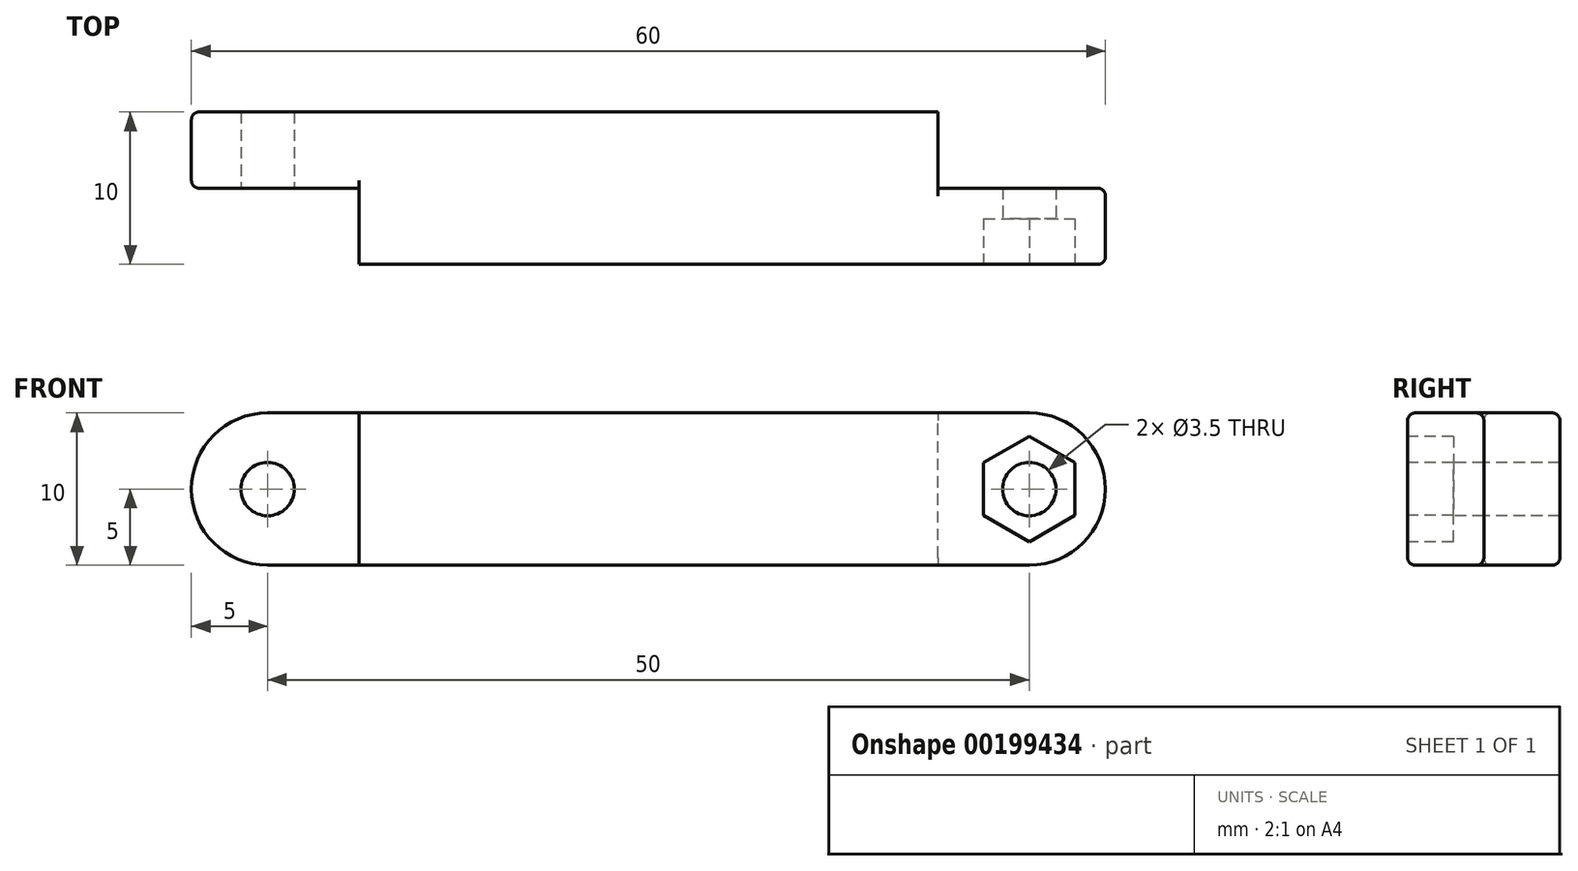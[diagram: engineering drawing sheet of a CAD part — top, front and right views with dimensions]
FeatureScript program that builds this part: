
annotation { "Feature Type Name" : "Feature", "Feature Type Description" : "" }
export const myFeature = defineFeature(function(context is Context, id is Id, definition is map)
    precondition{}
    {
        {
            var Q0;
            Q0=qCreatedBy(makeId("Front.planeOp"),FACE);
            var sketch = newSketch(context, id + "F0", { "sketchPlane" : qUnion([Q0])});
            skLineSegment(sketch, "E0.bottom", {"start": v(0, 0) * mm, "end": v(50, 0) * mm});
            skLineSegment(sketch, "E0.top", {"start": v(0, 10) * mm, "end": v(50, 10) * mm});
            skLineSegment(sketch, "E0.left", {"start": v(0, 0) * mm, "end": v(0, 10) * mm});
            skLineSegment(sketch, "E0.right", {"start": v(50, 0) * mm, "end": v(50, 10) * mm});
            skArc(sketch, "E1", {"start": v(0, 10) * mm, "mid": v(-5, 5) * mm, "end": v(0, 0) * mm});
            skArc(sketch, "E2", {"start": v(50, 0) * mm, "mid": v(55, 5) * mm, "end": v(50, 10) * mm});
            skSolve(sketch);
        }
        {
            var Q0;
            Q0 = qSketchRegion(id + "F0", true);
            extrude(context, id + "F1", {"entities" : qUnion([Q0]), "depth" : 10 * mm});
        }
        {
            var Q0;
            Q0=makeQuery(id+"F1.opExtrude","SWEPT_FACE",FACE,{"disambiguationData":[OSD([sQuery(id+"F0.wireOp",EDGE,"E0.top")])]});
            var sketch = newSketch(context, id + "F2", { "sketchPlane" : qUnion([Q0])});
            skLineSegment(sketch, "E3.bottom", {"start": v(-7.46, -5) * mm, "end": v(6, -5) * mm});
            skLineSegment(sketch, "E3.top", {"start": v(-7.46, -10) * mm, "end": v(6, -10) * mm});
            skLineSegment(sketch, "E3.left", {"start": v(-7.46, -5) * mm, "end": v(-7.46, -10) * mm});
            skLineSegment(sketch, "E3.right", {"start": v(6, -5) * mm, "end": v(6, -10) * mm});
            skLineSegment(sketch, "E4.bottom", {"start": v(44, -5) * mm, "end": v(57.28, -5) * mm});
            skLineSegment(sketch, "E4.top", {"start": v(44, 0) * mm, "end": v(57.28, 0) * mm});
            skLineSegment(sketch, "E4.left", {"start": v(44, 0) * mm, "end": v(44, -5) * mm});
            skLineSegment(sketch, "E4.right", {"start": v(57.28, 0) * mm, "end": v(57.28, -5) * mm});
            skSolve(sketch);
        }
        {
            var Q0;
            Q0 = qSketchRegion(id + "F2", true);
            extrude(context, id + "F3", {"entities" : qUnion([Q0]), "operationType" : NewBodyOperationType.REMOVE, "oppositeDirection" : true, "depth" : 25 * mm});
        }
        {
            var Q0;
            Q0=makeQuery(id+"F1.opExtrude","CAP_FACE",FACE,{"disambiguationData":[OSD([sQuery(id+"F0.wireOp",EDGE,"E0.bottom"),sQuery(id+"F0.wireOp",EDGE,"E0.top"),sQuery(id+"F0.wireOp",EDGE,"E1"),sQuery(id+"F0.wireOp",EDGE,"E2")])],"isStart":false});
            var sketch = newSketch(context, id + "F4", { "sketchPlane" : qUnion([Q0])});
            skCircle(sketch, "E5", {"center": v(50, 5) * mm, "radius": 1.75 * mm});
            skCircle(sketch, "E6", {"center": v(0, 5) * mm, "radius": 1.75 * mm});
            skPoint(sketch, "E6.centerSnap0", {"position": v(6, 5) * mm});
            skSolve(sketch);
        }
        {
            var Q0;
            Q0 = qSketchRegion(id + "F4", true);
            extrude(context, id + "F5", {"entities" : qUnion([Q0]), "operationType" : NewBodyOperationType.REMOVE, "oppositeDirection" : true, "depth" : 25 * mm});
        }
        {
            var Q0;
            Q0=makeQuery(id+"F1.opExtrude","CAP_FACE",FACE,{"disambiguationData":[OSD([sQuery(id+"F0.wireOp",EDGE,"E0.bottom"),sQuery(id+"F0.wireOp",EDGE,"E0.top"),sQuery(id+"F0.wireOp",EDGE,"E1"),sQuery(id+"F0.wireOp",EDGE,"E2")])],"isStart":false});
            var sketch = newSketch(context, id + "F6", { "sketchPlane" : qUnion([Q0])});
            skCircle(sketch, "E7.cCircle", {"center": v(50, 5) * mm, "radius": 3 * mm, "construction": true});
            skLineSegment(sketch, "E7.0", {"start": v(53, 6.73) * mm, "end": v(53, 3.27) * mm});
            skLineSegment(sketch, "E7.1", {"start": v(53, 3.27) * mm, "end": v(50, 1.54) * mm});
            skLineSegment(sketch, "E7.2", {"start": v(50, 1.54) * mm, "end": v(47, 3.27) * mm});
            skLineSegment(sketch, "E7.3", {"start": v(47, 3.27) * mm, "end": v(47, 6.73) * mm});
            skLineSegment(sketch, "E7.4", {"start": v(47, 6.73) * mm, "end": v(50, 8.46) * mm});
            skLineSegment(sketch, "E7.5", {"start": v(50, 8.46) * mm, "end": v(53, 6.73) * mm});
            skPoint(sketch, "E7.0.midPoint", {"position": v(53, 5) * mm});
            skSolve(sketch);
        }
        {
            var Q0;
            Q0 = qSketchRegion(id + "F6", true);
            extrude(context, id + "F7", {"entities" : qUnion([Q0]), "operationType" : NewBodyOperationType.REMOVE, "oppositeDirection" : true, "depth" : 3 * mm});
        }
        {
            var Q0;
            Q0=makeQuery(id+"F1.opExtrude","CAP_EDGE",EDGE,{"disambiguationData":[OSD([sQuery(id+"F0.wireOp",EDGE,"E0.top")])],"isStart":false});
            var Q1;
            Q1=makeQuery(id+"F1.opExtrude","CAP_EDGE",EDGE,{"disambiguationData":[OSD([sQuery(id+"F0.wireOp",EDGE,"E0.top")])],"isStart":true});
            var Q2;
            Q2=makeQuery(id+"F3.boolean.opBoolean","INTERSECT",EDGE,{"derivedFrom":[makeQuery(id+"F1.opExtrude","SWEPT_FACE",FACE,{"disambiguationData":[OSD([sQuery(id+"F0.wireOp",EDGE,"E1")])]}),makeQuery(id+"F3.opExtrude","SWEPT_FACE",FACE,{"disambiguationData":[OSD([sQuery(id+"F2.wireOp",EDGE,"E3.bottom")])]})]});
            var Q3;
            Q3=makeQuery(id+"F3.boolean.opBoolean","INTERSECT",EDGE,{"derivedFrom":[makeQuery(id+"F1.opExtrude","SWEPT_FACE",FACE,{"disambiguationData":[OSD([sQuery(id+"F0.wireOp",EDGE,"E1")])]}),makeQuery(id+"F3.opExtrude","SWEPT_FACE",FACE,{"disambiguationData":[OSD([sQuery(id+"F2.wireOp",EDGE,"P04TAq59-q1fG-UJBZ-M5Xo-CUCYvNxY8sxR.top")])]})]});
            var Q4;
            Q4=makeQuery(id+"F3.boolean.opBoolean","INTERSECT",EDGE,{"derivedFrom":[makeQuery(id+"F1.opExtrude","SWEPT_FACE",FACE,{"disambiguationData":[OSD([sQuery(id+"F0.wireOp",EDGE,"E2")])]}),makeQuery(id+"F3.opExtrude","SWEPT_FACE",FACE,{"disambiguationData":[OSD([sQuery(id+"F2.wireOp",EDGE,"E4.top")])]})]});
            var Q5;
            Q5=makeQuery(id+"F3.boolean.opBoolean","INTERSECT",EDGE,{"derivedFrom":[makeQuery(id+"F1.opExtrude","SWEPT_FACE",FACE,{"disambiguationData":[OSD([sQuery(id+"F0.wireOp",EDGE,"E2")])]}),makeQuery(id+"F3.opExtrude","SWEPT_FACE",FACE,{"disambiguationData":[OSD([sQuery(id+"F2.wireOp",EDGE,"E4.bottom")])]})]});
            fillet(context, id + "F8", {"entities" : qUnion([Q0, Q1, Q2, Q3, Q4, Q5]), "radius" : 0.5 * mm, "tangentPropagation" : true, "allowEdgeOverflow" : false});
        }
    });
